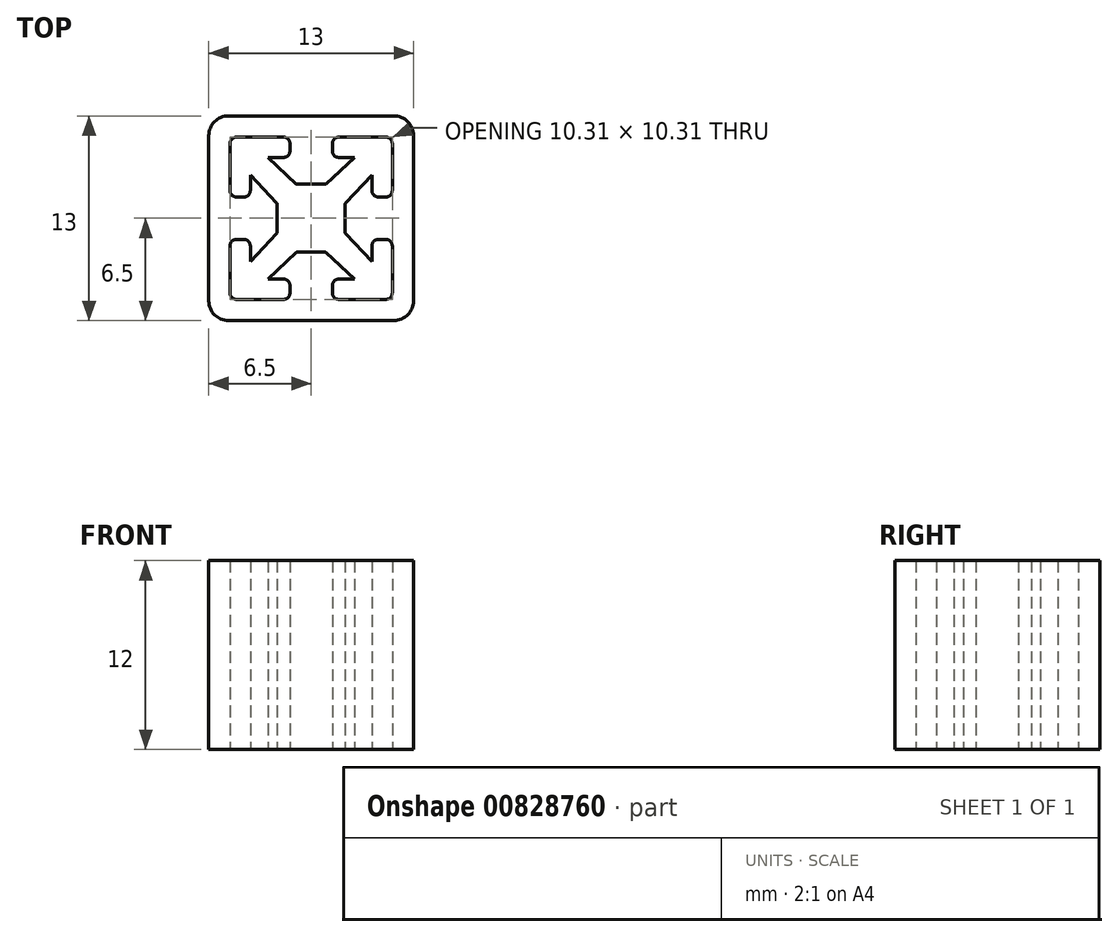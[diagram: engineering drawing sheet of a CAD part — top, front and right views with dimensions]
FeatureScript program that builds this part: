
annotation { "Feature Type Name" : "Feature", "Feature Type Description" : "" }
export const myFeature = defineFeature(function(context is Context, id is Id, definition is map)
    precondition{}
    {
        {
            var Q0;
            Q0=qCreatedBy(makeId("Top.planeOp"),FACE);
            var sketch = newSketch(context, id + "F0", { "sketchPlane" : qUnion([Q0])});
            skArc(sketch, "E0.0", {"start": v(6.5, 5.25) * mm, "mid": v(6.13, 6.13) * mm, "end": v(5.25, 6.5) * mm});
            skLineSegment(sketch, "E0.1", {"start": v(6.5, -5.25) * mm, "end": v(6.5, 5.25) * mm});
            skLineSegment(sketch, "E0.2", {"start": v(5.25, 6.5) * mm, "end": v(-5.25, 6.5) * mm});
            skArc(sketch, "E0.3", {"start": v(5.25, -6.5) * mm, "mid": v(6.13, -6.13) * mm, "end": v(6.5, -5.25) * mm});
            skArc(sketch, "E0.4", {"start": v(-5.25, 6.5) * mm, "mid": v(-6.13, 6.13) * mm, "end": v(-6.5, 5.25) * mm});
            skLineSegment(sketch, "E0.5", {"start": v(-6.5, 5.25) * mm, "end": v(-6.5, -5.25) * mm});
            skArc(sketch, "E0.6", {"start": v(-6.5, -5.25) * mm, "mid": v(-6.13, -6.13) * mm, "end": v(-5.25, -6.5) * mm});
            skLineSegment(sketch, "E0.7", {"start": v(-5.25, -6.5) * mm, "end": v(5.25, -6.5) * mm});
            skSolve(sketch);
        }
        {
            var Q0;
            Q0 = qSketchRegion(id + "F0", true);
            extrude(context, id + "F1", {"entities" : qUnion([Q0]), "endBound" : BoundingType.SYMMETRIC, "oppositeDirection" : true, "depth" : 12 * mm, "offsetDistance" : 25 * mm});
        }
        {
            var Q0;
            Q0=qCreatedBy(makeId("Top.planeOp"),FACE);
            var sketch = newSketch(context, id + "F2", { "sketchPlane" : qUnion([Q0])});
            skLineSegment(sketch, "E1.0", {"start": v(0.96, -2.18) * mm, "end": v(2.75, -3.86) * mm});
            skArc(sketch, "E1.1", {"start": v(0.96, -2.18) * mm, "mid": v(0.93, -2.16) * mm, "end": v(0.89, -2.16) * mm});
            skLineSegment(sketch, "E1.2", {"start": v(0.89, -2.16) * mm, "end": v(-0.89, -2.16) * mm});
            skArc(sketch, "E1.3", {"start": v(-0.89, -2.16) * mm, "mid": v(-0.93, -2.16) * mm, "end": v(-0.96, -2.18) * mm});
            skLineSegment(sketch, "E1.4", {"start": v(-0.96, -2.18) * mm, "end": v(-2.75, -3.86) * mm});
            skLineSegment(sketch, "E1.5", {"start": v(-2.75, -3.86) * mm, "end": v(-1.75, -3.86) * mm});
            skArc(sketch, "E1.6", {"start": v(-1.35, -4.27) * mm, "mid": v(-1.47, -3.98) * mm, "end": v(-1.75, -3.86) * mm});
            skLineSegment(sketch, "E1.7", {"start": v(-1.35, -4.27) * mm, "end": v(-1.35, -4.75) * mm});
            skArc(sketch, "E1.8", {"start": v(-1.75, -5.15) * mm, "mid": v(-1.47, -5.04) * mm, "end": v(-1.35, -4.75) * mm});
            skLineSegment(sketch, "E1.9", {"start": v(-1.75, -5.15) * mm, "end": v(-4.75, -5.15) * mm});
            skArc(sketch, "E1.10", {"start": v(-5.15, -4.75) * mm, "mid": v(-5.04, -5.04) * mm, "end": v(-4.75, -5.15) * mm});
            skLineSegment(sketch, "E1.11", {"start": v(-5.15, -1.75) * mm, "end": v(-5.15, -4.75) * mm});
            skArc(sketch, "E1.12", {"start": v(-4.75, -1.35) * mm, "mid": v(-5.04, -1.47) * mm, "end": v(-5.15, -1.75) * mm});
            skLineSegment(sketch, "E1.13", {"start": v(-4.27, -1.35) * mm, "end": v(-4.75, -1.35) * mm});
            skArc(sketch, "E1.14", {"start": v(-3.86, -1.75) * mm, "mid": v(-3.98, -1.47) * mm, "end": v(-4.27, -1.35) * mm});
            skLineSegment(sketch, "E1.15", {"start": v(-3.86, -2.75) * mm, "end": v(-3.86, -1.75) * mm});
            skLineSegment(sketch, "E1.16", {"start": v(-2.18, -0.96) * mm, "end": v(-3.86, -2.75) * mm});
            skArc(sketch, "E1.17", {"start": v(-2.18, -0.96) * mm, "mid": v(-2.16, -0.93) * mm, "end": v(-2.16, -0.89) * mm});
            skArc(sketch, "E1.18", {"start": v(5.15, 4.75) * mm, "mid": v(5.04, 5.04) * mm, "end": v(4.75, 5.15) * mm});
            skLineSegment(sketch, "E1.19", {"start": v(5.15, 1.75) * mm, "end": v(5.15, 4.75) * mm});
            skArc(sketch, "E1.20", {"start": v(4.75, 1.35) * mm, "mid": v(5.04, 1.47) * mm, "end": v(5.15, 1.75) * mm});
            skLineSegment(sketch, "E1.21", {"start": v(4.27, 1.35) * mm, "end": v(4.75, 1.35) * mm});
            skArc(sketch, "E1.22", {"start": v(3.86, 1.75) * mm, "mid": v(3.98, 1.47) * mm, "end": v(4.27, 1.35) * mm});
            skLineSegment(sketch, "E1.23", {"start": v(3.86, 2.75) * mm, "end": v(3.86, 1.75) * mm});
            skLineSegment(sketch, "E1.24", {"start": v(2.18, 0.96) * mm, "end": v(3.86, 2.75) * mm});
            skArc(sketch, "E1.25", {"start": v(2.18, 0.96) * mm, "mid": v(2.16, 0.93) * mm, "end": v(2.16, 0.89) * mm});
            skLineSegment(sketch, "E1.26", {"start": v(2.16, 0.89) * mm, "end": v(2.16, -0.89) * mm});
            skArc(sketch, "E1.27", {"start": v(2.16, -0.89) * mm, "mid": v(2.16, -0.93) * mm, "end": v(2.18, -0.96) * mm});
            skLineSegment(sketch, "E1.28", {"start": v(2.18, -0.96) * mm, "end": v(3.86, -2.75) * mm});
            skLineSegment(sketch, "E1.29", {"start": v(3.86, -2.75) * mm, "end": v(3.86, -1.75) * mm});
            skArc(sketch, "E1.30", {"start": v(1.35, -4.75) * mm, "mid": v(1.47, -5.04) * mm, "end": v(1.75, -5.15) * mm});
            skLineSegment(sketch, "E1.31", {"start": v(1.35, -4.27) * mm, "end": v(1.35, -4.75) * mm});
            skArc(sketch, "E1.32", {"start": v(1.75, -3.86) * mm, "mid": v(1.47, -3.98) * mm, "end": v(1.35, -4.27) * mm});
            skLineSegment(sketch, "E1.33", {"start": v(2.75, -3.86) * mm, "end": v(1.75, -3.86) * mm});
            skLineSegment(sketch, "E1.34", {"start": v(1.75, -5.15) * mm, "end": v(4.75, -5.15) * mm});
            skArc(sketch, "E1.35", {"start": v(4.75, -5.15) * mm, "mid": v(5.04, -5.04) * mm, "end": v(5.15, -4.75) * mm});
            skLineSegment(sketch, "E1.36", {"start": v(5.15, -1.75) * mm, "end": v(5.15, -4.75) * mm});
            skArc(sketch, "E1.37", {"start": v(5.15, -1.75) * mm, "mid": v(5.04, -1.47) * mm, "end": v(4.75, -1.35) * mm});
            skLineSegment(sketch, "E1.38", {"start": v(4.27, -1.35) * mm, "end": v(4.75, -1.35) * mm});
            skArc(sketch, "E1.39", {"start": v(4.27, -1.35) * mm, "mid": v(3.98, -1.47) * mm, "end": v(3.86, -1.75) * mm});
            skLineSegment(sketch, "E1.40", {"start": v(1.75, 5.15) * mm, "end": v(4.75, 5.15) * mm});
            skArc(sketch, "E1.41", {"start": v(1.75, 5.15) * mm, "mid": v(1.47, 5.04) * mm, "end": v(1.35, 4.75) * mm});
            skLineSegment(sketch, "E1.42", {"start": v(1.35, 4.27) * mm, "end": v(1.35, 4.75) * mm});
            skArc(sketch, "E1.43", {"start": v(1.35, 4.27) * mm, "mid": v(1.47, 3.98) * mm, "end": v(1.75, 3.86) * mm});
            skLineSegment(sketch, "E1.44", {"start": v(2.75, 3.86) * mm, "end": v(1.75, 3.86) * mm});
            skLineSegment(sketch, "E1.45", {"start": v(0.96, 2.18) * mm, "end": v(2.75, 3.86) * mm});
            skArc(sketch, "E1.46", {"start": v(0.89, 2.16) * mm, "mid": v(0.93, 2.16) * mm, "end": v(0.96, 2.18) * mm});
            skLineSegment(sketch, "E1.47", {"start": v(-0.89, 2.16) * mm, "end": v(0.89, 2.16) * mm});
            skArc(sketch, "E1.48", {"start": v(-0.96, 2.18) * mm, "mid": v(-0.93, 2.16) * mm, "end": v(-0.89, 2.16) * mm});
            skLineSegment(sketch, "E1.49", {"start": v(-0.96, 2.18) * mm, "end": v(-2.75, 3.86) * mm});
            skLineSegment(sketch, "E1.50", {"start": v(-2.75, 3.86) * mm, "end": v(-1.75, 3.86) * mm});
            skArc(sketch, "E1.51", {"start": v(-1.75, 3.86) * mm, "mid": v(-1.47, 3.98) * mm, "end": v(-1.35, 4.27) * mm});
            skLineSegment(sketch, "E1.52", {"start": v(-1.35, 4.27) * mm, "end": v(-1.35, 4.75) * mm});
            skArc(sketch, "E1.53", {"start": v(-1.35, 4.75) * mm, "mid": v(-1.47, 5.04) * mm, "end": v(-1.75, 5.15) * mm});
            skLineSegment(sketch, "E1.54", {"start": v(-1.75, 5.15) * mm, "end": v(-4.75, 5.15) * mm});
            skArc(sketch, "E1.55", {"start": v(-4.75, 5.15) * mm, "mid": v(-5.04, 5.04) * mm, "end": v(-5.15, 4.75) * mm});
            skLineSegment(sketch, "E1.56", {"start": v(-5.15, 1.75) * mm, "end": v(-5.15, 4.75) * mm});
            skArc(sketch, "E1.57", {"start": v(-5.15, 1.75) * mm, "mid": v(-5.04, 1.47) * mm, "end": v(-4.75, 1.35) * mm});
            skLineSegment(sketch, "E1.58", {"start": v(-4.27, 1.35) * mm, "end": v(-4.75, 1.35) * mm});
            skArc(sketch, "E1.59", {"start": v(-4.27, 1.35) * mm, "mid": v(-3.98, 1.47) * mm, "end": v(-3.86, 1.75) * mm});
            skLineSegment(sketch, "E1.60", {"start": v(-3.86, 2.75) * mm, "end": v(-3.86, 1.75) * mm});
            skLineSegment(sketch, "E1.61", {"start": v(-2.18, 0.96) * mm, "end": v(-3.86, 2.75) * mm});
            skArc(sketch, "E1.62", {"start": v(-2.16, 0.89) * mm, "mid": v(-2.16, 0.93) * mm, "end": v(-2.18, 0.96) * mm});
            skLineSegment(sketch, "E1.63", {"start": v(-2.16, 0.89) * mm, "end": v(-2.16, -0.89) * mm});
            skSolve(sketch);
        }
        {
            var Q0;
            Q0=makeQuery(id+"F2.imprint","IMPRINT",FACE,{"disambiguationData":[TD([[makeQuery(id+"F2.imprint","IMPRINT",EDGE,{"derivedFrom":sQuery(id+"F2.wireOp",EDGE,"E1.0")}),1.0]])]});
            extrude(context, id + "F3", {"entities" : qUnion([Q0]), "operationType" : NewBodyOperationType.REMOVE, "endBound" : BoundingType.SYMMETRIC, "depth" : 20 * mm, "offsetDistance" : 25 * mm});
        }
    });
